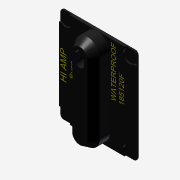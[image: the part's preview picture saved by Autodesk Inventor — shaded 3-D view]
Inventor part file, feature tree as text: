
AUTODESK INVENTOR PART (.ipt)
format: ipt  version: 2014 (Build 180170000, 170)  size: 659,456 bytes
history: native  units: mm (DEFAULTED — no unit token found)
features: sketch x6, extrude x4, plane x2, mirror x2, emboss x2, chamfer x1, reference x1
ambient origin geometry x8: Origin, YZ Plane, XZ Plane, XY Plane, X Axis, Y Axis, Z Axis, Center Point
bodies: Solid1 (feature_tree)
feature tree (18):
  extrude  "Extrusion1"  Depth=6.35mm
  extrude  "Extrusion2"  Depth=2.54mm
  chamfer  "Chamfer2"  Distance=8.89mm
  extrude  "Extrusion3"  Depth=0.762mm
  plane  "Work Plane1"
  plane  "Work Plane2"
  extrude  "Extrusion5"  Depth=0.0508mm TaperAngle=0.0deg
  mirror  "Mirror3"
  mirror  "Mirror4"
  emboss  "Emboss1"
  emboss  "Emboss2"
  sketch  "Sketch1"  dims[d0=1.524mm d1=0.0mm d2=6.35mm]
  reference  "Reference1"
  sketch  "Sketch2"  dims[d3=8.89mm d4=0.0mm d7=3.81mm d8=2.54mm]
  sketch  "Sketch3"  dims[d10=2.159mm]
  sketch  "Sketch5"  dims[d11=7.62mm d12=8.89mm d13=0.0mm]
  sketch  "Sketch6"  dims[d17=6.35mm d18=0.762mm]
  sketch  "Sketch7"  dims[d19=0.762mm d20=0.762mm d21=0.0mm d22=0.0508mm d23=0.0mm d24=0.0508mm d25=0.0mm d26=45.0deg]
